# Revit family: EDLQ-195-1100-xxx-W
name_source: partatom
category: Oprawy oświetleniowe
revit_build: Autodesk Revit 2017 (Build: 20190507_1515(x64)
units: mm (PartAtom-declared; Revit-internal decimal feet)

## family parameters
Numer OmniClass = 23.80.70.11
Obiekt nadrzędny = Powierzchnia
Punkt obliczania pomieszczeń = Nie
Tnij formami wycięć po wczytaniu = Nie
Typ części = Normalny
Tytuł OmniClass = Luminaries for Internal Lighting
Współdzielony = Nie
Wymiar okrągłego złącza = Użyj średnicy
Źródło światła = Tak

## types (4) — shared parameters
Emituj kształt widoczny w renderingu = Nie
Emituj z długości prostokąta = 170 mm  [stored 0.557743 ft]
Emituj z szerokości prostokąta = 170 mm  [stored 0.557743 ft]
Filtr koloru = 16777215
Kod zespołu = D5020200
Lampa = LED
Obciążenie pozorne = 8 VA
Odchylenie kierunku = 90.00°
Plik sieci fotometrycznej = EDLQ 1951100-840 W.IES
Producent = RIDI Leuchten GmbH
URL = www.ridi.de
Zmiana temperatury barwowej przyciemniania lampy = <Brak>
brand = RIDI
conformity mark = CE
electrical safety class = 1
height = 75 mm
ingress protection (IP) code = IP20
length = 195 mm  [stored 0.639764 ft]
nominal frequency = 50-60Hz
nominal voltage = 230
rated input power = 8
voltage type (AC, DC, UC) = AC
width = 195 mm  [stored 0.639764 ft]
zero-valued in all types: Domyślna rzędna

## per-type parameters (varying)
| type | Model | weight |
| EDLQ 195/1100-840 W | 0321341 | 1,26 kg |
| EDLQ 195/1100-840 W-DALI | 0331341 | 1,3 kg |
| EDLQ 195/1100-830 W | 0321342 | 1,26 kg |
| EDLQ 195/1100-830 W-DALI | 0331342 | 1,3 kg |

note: column(s) folded — value = type name in every type: product name

note: [stored X ft] marks values corroborated as IEEE doubles in the binary element streams (Revit-internal decimal feet)
